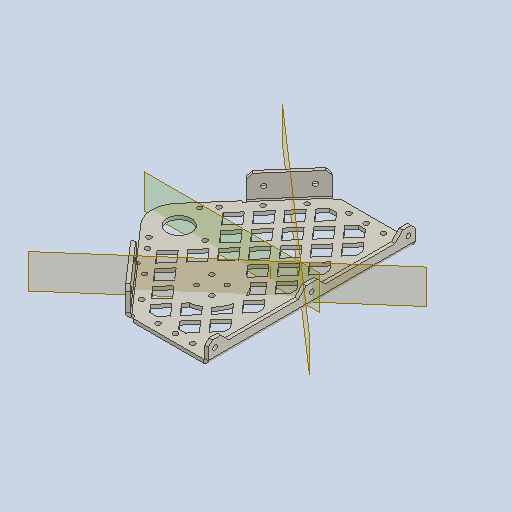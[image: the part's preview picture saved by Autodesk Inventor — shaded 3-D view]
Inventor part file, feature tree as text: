
AUTODESK INVENTOR PART (.ipt)
format: ipt  version: 2022 (Build 260153000, 153)  size: 833,536 bytes
history: native  units: in
note: dims shown in document units (in); Inventor stores cm internally (conversion verified against a paired STEP export)
features: other x17, sketch x15, sheet_metal_op x14, hole x7, plane x5, projected_geometry x4, reference x4, extrude x2, fillet x1, mirror x1
ambient origin geometry x8: Origin, YZ Plane, XZ Plane, XY Plane, X Axis, Y Axis, Z Axis, Center Point
bodies: Solid1 (feature_tree)
feature tree (70):
  sheet_metal_op  "Face1"
  other  "Work Axis1"
  sheet_metal_op  "Face2"
  sheet_metal_op  "Flange1"
  sheet_metal_op  "Flange2"
  sheet_metal_op  "Flange3"
  other  "Corner Chamfer1"
  hole  "Hole1"  [1 undecoded]
  extrude  "Extrusion1"  Depth=0.7874in
  extrude  "Extrusion2"  Depth=0.0312in
  hole  "Hole2"  [1 undecoded]
  hole  "Hole3"  [1 undecoded]
  hole  "Hole4"  [1 undecoded]
  plane  "Work Plane3"
  plane  "Work Plane4"
  plane  "Work Plane5"
  hole  "Hole5"  [1 undecoded]
  hole  "Hole6"  [1 undecoded]
  hole  "Hole7"  [1 undecoded]
  sheet_metal_op  "Face4"
  fillet  "Fillet1"  Radius=0.1024in
  mirror  "Mirror1"
  sketch  "Sketch1"  dims[d0=2.1654in d1=6.0in]
  other  "Plate1"
  plane  "Work Plane1"
  plane  "Work Plane2"
  sketch  "Sketch2"  dims[d2=0.1024in d3=0.7874in]
  other  "Plate2"
  sheet_metal_op  "Bend1"
  sketch  "Sketch3"  dims[d4=1.5748in d6=0.0312in]
  other  "Plate3"
  sheet_metal_op  "Bend2"
  sheet_metal_op  "Corner1"
  sketch  "Sketch4"  dims[d7=0.1024in d8=0.0512in]
  other  "Plate4"
  sheet_metal_op  "Bend3"
  sheet_metal_op  "Corner2"
  sketch  "Sketch5"  dims[d9=0.2047in d10=0.0312in]
  other  "Plate5"
  sheet_metal_op  "Bend4"
  sheet_metal_op  "Corner3"
  sketch  "Sketch6"  dims[d11=0.1024in d12=0.0512in]
  sketch  "Sketch7"  dims[d13=0.2047in d14=0.0312in]
  projected_geometry  "Projected Loop1"
  sketch  "Sketch8"  dims[d15=0.5906in d16=90.0deg d17=0.0312in d18=0.3071in]
  reference  "Reference1"
  sketch  "Sketch9"  dims[d19=0.0512in d20=0.0312in d21=0.1024in]
  reference  "Reference2"
  reference  "Reference3"
  reference  "Reference4"
  sketch  "Sketch12"  dims[d22=0.0512in]
  sketch  "Sketch13"  dims[d23=0.2047in]
  sketch  "Sketch14"  dims[d24=0.0312in]
  projected_geometry  "Projected Loop2"
  sketch  "Sketch15"  dims[d25=1.75in d26=0.1in]
  sketch  "Sketch16"  dims[d27=0.7819in d28=90.0deg d29=0.0312in]
  projected_geometry  "Projected Loop3"
  other  "Plate7"
  sheet_metal_op  "Bend6"
  sketch  "Sketch18"  dims[d30=0.3071in d31=0.0512in d32=0.0312in d33=0.1024in d34=0.0512in d35=0.2047in d36=0.0312in d37=1.75in d38=0.1in d39=0.7819in d40=90.0deg d41=0.0312in d42=0.3071in d43=0.0512in d44=0.0312in d45=0.125in d46=0.25in d47=45.0deg d48=0.7087in d49=0.75in d50=0.248in d51=0.25in d52=90.0deg d53=0.1024in d54=0.8108in d55=0.3937in d56=0.1969in d57=0.3937in d58=0.3937in d59=0.3937in d60=0.1969in d64=0.1969in d67=0.1969in d68=0.1969in d69=0.1969in d70=0.1969in d71=0.1969in d72=0.1969in d73=0.1969in d74=0.1969in d75=0.4329in d76=0.4329in d77=0.4329in d78=0.4329in d79=0.4329in d80=0.4329in d81=0.4048in d82=0.1969in d83=0.4329in d84=0.4329in d85=0.1969in d86=0.1969in d87=0.1969in d88=0.1969in d89=0.1969in d90=0.1969in d91=0.1969in d92=0.1969in d93=0.1969in d94=0.4329in d95=0.4329in d96=0.4329in d97=0.4329in d98=0.4329in d99=0.4329in d100=0.4329in d101=0.1969in d102=1.0in d103=0.0in d104=1.5748in d105=0.748in d106=0.6299in d107=45.0deg d113=1.0in d114=0.0in d115=0.142in d116=0.75in d117=0.248in d118=0.25in d119=90.0deg d120=1.0in d121=0.8108in d122=0.1417in d123=0.75in d124=0.375in d125=0.25in d126=0.5635in d127=0.1024in d128=0.0in d129=0.142in d130=0.75in d131=0.248in d132=0.25in d133=90.0deg d134=0.1024in d135=0.0in d136=0.1339in d137=0.75in d138=0.248in d139=0.25in d140=90.0deg d141=0.1024in d142=0.8108in d143=0.1339in d144=0.75in d145=0.375in d146=0.25in d147=0.5635in d148=0.1024in d149=0.8108in d150=0.2362in d151=0.2362in d152=0.2362in d153=0.2362in d154=0.408in d155=0.408in d156=0.408in d157=0.408in d158=0.408in d159=0.408in d160=0.408in d161=0.408in d162=0.408in d163=0.408in d168=0.1024in d169=0.0in d170=0.408in d171=0.408in d172=0.1969in d173=0.1969in d174=0.134in d175=0.75in d176=0.248in d177=0.25in d178=90.0deg d179=0.1024in d180=0.8108in d181=0.3937in d182=0.1969in d183=0.0312in d184=0.1024in d185=0.0512in d186=0.2047in d187=0.0312in d188=0.0625in d199=0.3937in d200=135.0deg d201=0.3937in d202=0.3937in d203=0.3937in d204=0.1024in d205=0.0in]
  projected_geometry  "Projected Loop5"
  other  "Cut1"
  other  "Cut3"
  parser-record x1  (decoder bookkeeping rows leaked as tree rows — omitted from the tree; the rows remain in map.json)
  other  "Main Body.iam"
  other  "Brushless Motor:1"
  other  "Top Stubstructure:1"
  other  "Mount Side:2"
  other  "Mount Side:1"
  other  "Definition1"
note: 7 required parameter values undecoded (feature->parameter linkage not recoverable at this tier; creation-order binding heuristic only, values carry confidence <= 0.55)
note: 1 file-system path scrubbed to <path> (originals preserved in map.json)
